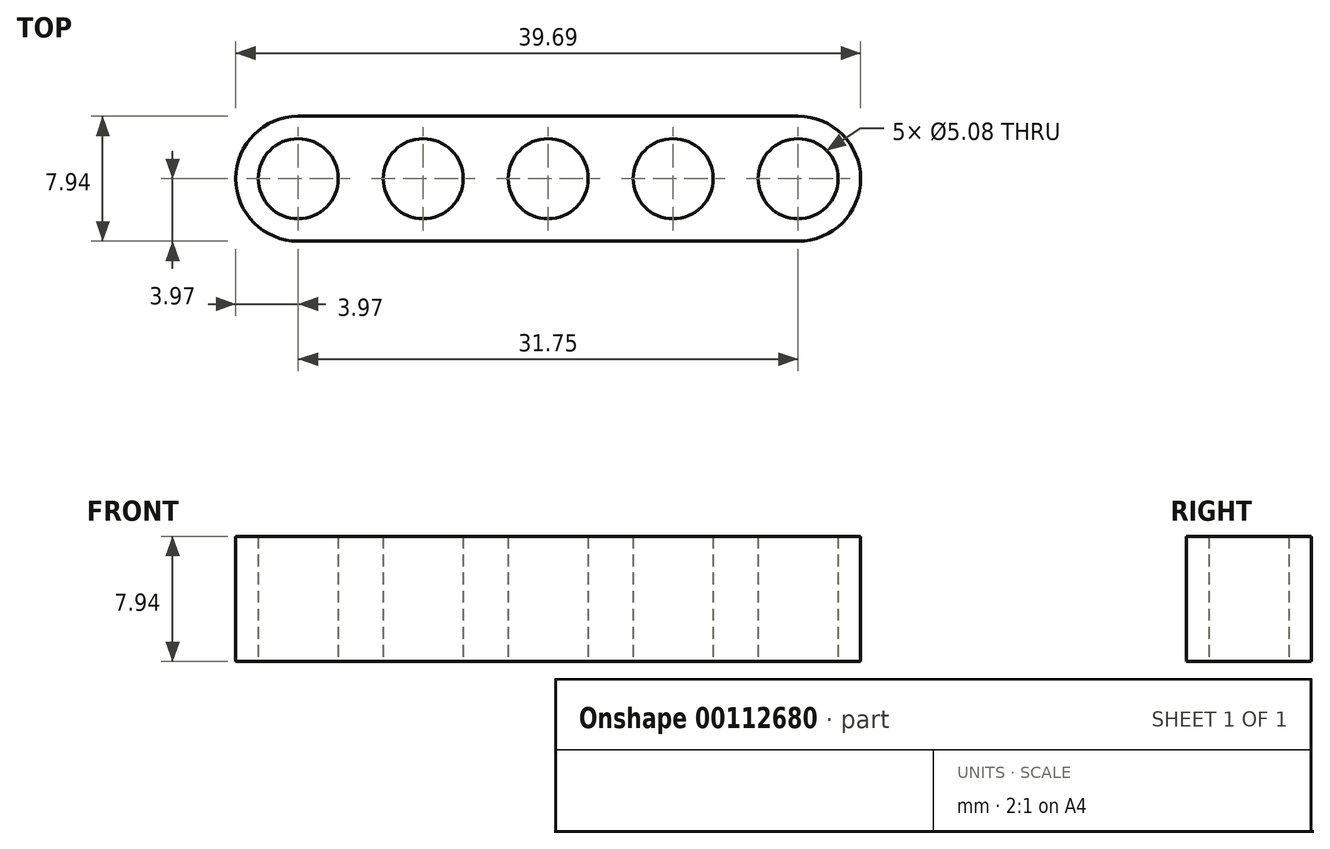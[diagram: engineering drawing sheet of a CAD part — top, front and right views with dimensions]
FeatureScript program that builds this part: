
annotation { "Feature Type Name" : "Feature", "Feature Type Description" : "" }
export const myFeature = defineFeature(function(context is Context, id is Id, definition is map)
    precondition{}
    {
        {
            var Q0;
            Q0=qCreatedBy(makeId("Top.planeOp"),FACE);
            var sketch = newSketch(context, id + "F0", { "sketchPlane" : qUnion([Q0])});
            skLineSegment(sketch, "E0", {"start": v(0, 0) * mm, "end": v(7.94, 0) * mm, "construction": true});
            skLineSegment(sketch, "E1", {"start": v(7.94, 0) * mm, "end": v(15.88, 0) * mm, "construction": true});
            skLineSegment(sketch, "E2", {"start": v(15.88, 0) * mm, "end": v(23.81, 0) * mm, "construction": true});
            skLineSegment(sketch, "E3", {"start": v(23.81, 0) * mm, "end": v(31.75, 0) * mm, "construction": true});
            skLineSegment(sketch, "E4.bottom", {"start": v(0, 3.97) * mm, "end": v(31.75, 3.97) * mm});
            skLineSegment(sketch, "E4.top", {"start": v(0, -3.97) * mm, "end": v(31.75, -3.97) * mm});
            skLineSegment(sketch, "E4.left", {"start": v(0, 3.97) * mm, "end": v(0, -3.97) * mm});
            skLineSegment(sketch, "E4.right", {"start": v(31.75, 3.97) * mm, "end": v(31.75, -3.97) * mm});
            skArc(sketch, "E5", {"start": v(0, 3.97) * mm, "mid": v(-3.97, 0) * mm, "end": v(0, -3.97) * mm});
            skArc(sketch, "E6", {"start": v(31.75, -3.97) * mm, "mid": v(35.72, 0) * mm, "end": v(31.75, 3.97) * mm});
            skCircle(sketch, "E7", {"center": v(0, 0) * mm, "radius": 2.54 * mm});
            skCircle(sketch, "E8", {"center": v(7.94, 0) * mm, "radius": 2.54 * mm});
            skCircle(sketch, "E9", {"center": v(15.88, 0) * mm, "radius": 2.54 * mm});
            skCircle(sketch, "E10", {"center": v(23.81, 0) * mm, "radius": 2.54 * mm});
            skCircle(sketch, "E11", {"center": v(31.75, 0) * mm, "radius": 2.54 * mm});
            skSolve(sketch);
        }
        {
            var Q0;
            Q0 = qSketchRegion(id + "F0", true);
            extrude(context, id + "F1", {"entities" : qUnion([Q0]), "depth" : 7.94 * mm});
        }
    });
